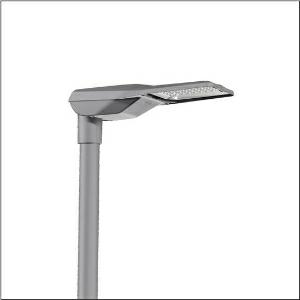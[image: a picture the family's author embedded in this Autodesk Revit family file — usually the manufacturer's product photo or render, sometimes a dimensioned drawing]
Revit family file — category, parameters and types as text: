
# Revit family: streetlight_sl_21_iq_mini___st1_5a_5xe2p41g08gb_fe87
name_source: partatom
category: Lighting Fixtures
units: mm (PartAtom-declared; Revit-internal decimal feet)

## family parameters
Cut with Voids When Loaded = No
Host = Face
Light Source = No
Part Type = Normal
Room Calculation Point = No
Round Connector Dimension = Use Diameter
Shared = No

## types (1)
- --- (1 x LED, 5810 lm, 37.1 W, 4000K)
    Apparent Load = 37 VA
    CIE Flux Codes = 22 53 95 100 100
    Color Rendering = 70
    Color Temperature = 4000K
    Default Elevation = 1800 mm
    Description = Streetlight SL 21 iQ mini, mast luminaire, primary light control with lens, of PMMA, primary optical cover: cover, of toughened safety glass, transparent, light distribution: ST1.5a, light emission: direct distribution, primary light characteristic: asymmetric, installation type: post-top, side-entry, LED, High Power LED, rated luminous flux: 5.810lm, luminous efficacy: 157lm/W, light colour: 740, colour temperature: 4000K, control gear: iQ Street-Remote, control: Street-Remote, Auto-Match, Temp-Guard, Lumen-Switch, Night-Set, Smart-Wire, Light-Fading, Desk-Remote (wireless, voltage-free reading and setting of iQ features in the workshop via application-optimized NFC function/RFID function), optimised constant luminous flux control (CLO 2.0), pre-setting: linear dimming characteristic, mains connection: 220..240V, AC, 50/60Hz, start of lifetime: 37W, end of service life: 39W, reduction: 18W, luminaire housing, of diecast aluminium, powder-coated, Siteco® metallic grey (DB 702S), corrosivity category C5 mid according to DIN EN ISO 12944, please order mast flange separately, inclination adjustable: 0°, 5°, 10°, 15°, sealing non-destructively replaceable, multi-level sealing system, length: 628mm, width: 235mm, height: 110mm, mast flange for spigot size: 42mm (side-entry): 5XC10008XM4, 60/48mm (side-entry/post-top): 5XC10108XM2, 76/60mm (side-entry/post-top): 5XC10108XM1, mounting height: 4..8m, protection rating (complete): IP66, insulation class (complete): insulation class II (safety insulation), certification: CE, ENEC, ENEC+, VDE, impact resistance: IK10, permissible operating ambient temperature for outdoor applications: -40..+50°C, standard-compliant lighting for roads and squares, packaging unit: 1 piece

Light Distribution: ST1.5a
    Height = 110 mm
    Lamp = 1 x LED
    Lamp Light Flux = 5810 lm
    Lamp Power = 37.1 W
    Lamp count = 1
    Length = 625 mm
    Luminous efficacy = 157 lm/W
    Manufacturer = Siteco
    ModVariant = No
    Model = 5XE2P41G08GB
    Number of Poles = 1
    OnlyDefault = Yes
    Power Factor = 1
    Product Name = Streetlight SL 21 iQ mini | ST1.5a
    Product group = mast luminaire | pylon top
    ProductGroupID = 6100
    Protection Class = Protection class II
    Protection Degree = IP 66
    RLX_Detail_Level = 1
    RLX_Emergency_Light_Flux = 0 lm
    RLX_Emergency_Type = 0
    RLX_Emergency_Type_DB = No
    RlxData = <blob elided: 29897 chars, md5=368fedd1>
    Socket = socket
    Standby Power = 0 W
    System Light Flux = 5810 lm
    System Power = 37 W
    Type Comments = factory setting: luminous flux: 100 % | dim-lin: 254 | 385 mA
    Type Image = l_1003519.jpg
    URL = http://relux.com
    VarID = @adj_175752
    Voltage = 0 V
    Weight = 0.00 kg
    Width = 234 mm

## geometry (parser evidence)
native form markers: Blend x4, Sweep x9
no freeform markers — native parametric forms only
